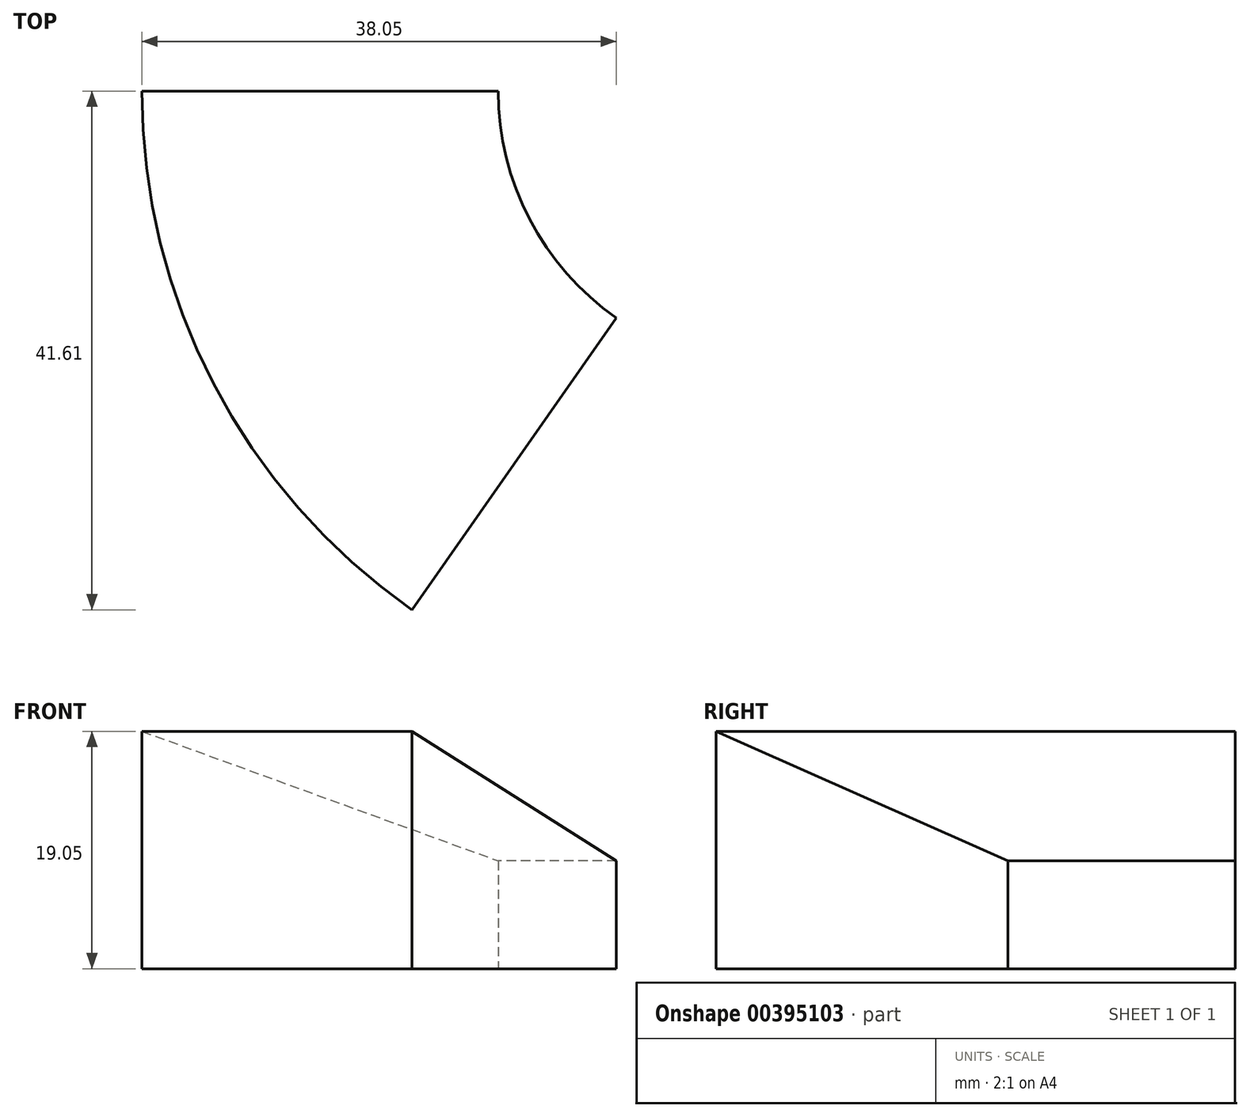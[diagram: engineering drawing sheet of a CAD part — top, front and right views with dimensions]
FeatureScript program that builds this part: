
annotation { "Feature Type Name" : "Feature", "Feature Type Description" : "" }
export const myFeature = defineFeature(function(context is Context, id is Id, definition is map)
    precondition{}
    {
        {
            var Q0;
            Q0=qCreatedBy(makeId("Front.planeOp"),FACE);
            var sketch = newSketch(context, id + "F0", { "sketchPlane" : qUnion([Q0])});
            skLineSegment(sketch, "E0", {"start": v(0, 0) * mm, "end": v(0, 25.26) * mm, "construction": true});
            skLineSegment(sketch, "E1", {"start": v(-50.8, 0) * mm, "end": v(-50.8, 19.05) * mm});
            skLineSegment(sketch, "E2", {"start": v(-50.8, 19.05) * mm, "end": v(-22.23, 8.65) * mm});
            skLineSegment(sketch, "E3", {"start": v(-22.23, 8.65) * mm, "end": v(-22.23, 0) * mm});
            skLineSegment(sketch, "E4", {"start": v(-22.23, 0) * mm, "end": v(-50.8, 0) * mm});
            skSolve(sketch);
        }
        {
            var Q0;
            Q0=makeQuery(id+"F0.imprint","IMPRINT",FACE,{"disambiguationData":[TD([[makeQuery(id+"F0.imprint","IMPRINT",EDGE,{"derivedFrom":sQuery(id+"F0.wireOp",EDGE,"E1")}),-1.0]])]});
            var Q1;
            Q1=sQuery(id+"F0.wireOp",EDGE,"E0");
            revolve(context, id + "F1", {"entities" : qUnion([Q0]), "axis" : qUnion([Q1]), "revolveType" : RevolveType.ONE_DIRECTION, "angle" : 55 * degree});
        }
    });
